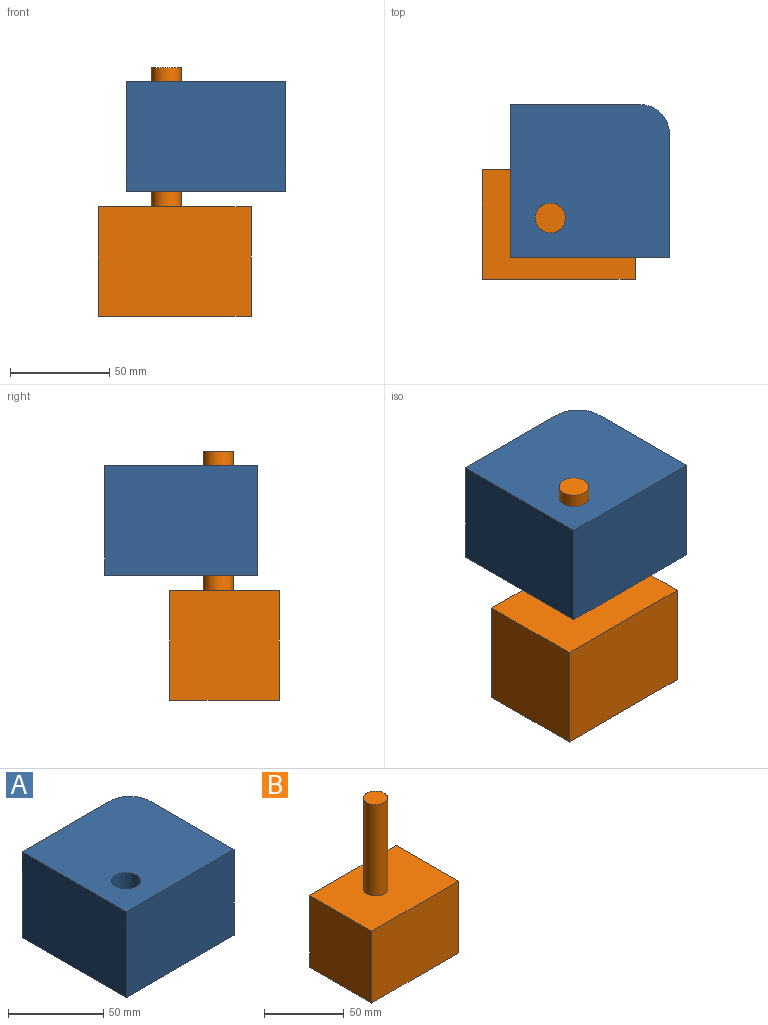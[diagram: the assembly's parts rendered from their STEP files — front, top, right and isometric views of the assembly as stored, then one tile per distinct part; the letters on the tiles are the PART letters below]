
ASSEMBLY  parts=2 mates=1
PART A: 8 faces, bbox 80x77.1x55 mm
  f0: plane 65x55mm, normal (0,1,0), area 3575mm2, adj f1,f4,f5,f7
  f1: plane 77.05x55mm, normal (-1,0,0), area 4237.9mm2, adj f0,f2,f4,f5
  f2: plane 80x55mm, normal (0,-1,0), area 4400mm2, adj f1,f3,f4,f5
  f3: plane 62.05x55mm, normal (1,0,0), area 3412.9mm2, adj f2,f4,f5,f7
  f4: plane 80x77.05mm, normal (0,0,1), area 5939.2mm2, adj f0,f1,f2,f3,f6,f7
  f5: plane 80x77.05mm, normal (0,0,-1), area 5939.2mm2, adj f0,f1,f2,f3,f6,f7
  f6: cylinder r=7.5mm len=55mm, axis (0,0,-1), area 2591.8mm2, adj f4,f5
  f7: cylinder r=15mm len=55mm, axis (0,0,-1), area 1295.9mm2, adj f0,f3,f4,f5
PART B: 8 faces, bbox 76.7x55x124.9 mm
  f0: plane 55x55mm, normal (-1,0,0), area 3025mm2, adj f1,f3,f4,f5
  f1: plane 76.74x55mm, normal (0,0,-1), area 4220.6mm2, adj f0,f2,f4,f5
  f2: plane 55x55mm, normal (1,0,0), area 3025mm2, adj f1,f3,f4,f5
  f3: plane 76.74x55mm, normal (0,0,1), area 4043.9mm2, adj f0,f2,f4,f5,f6
  f4: plane 76.74x55mm, normal (0,-1,0), area 4220.6mm2, adj f0,f1,f2,f3
  f5: plane 76.74x55mm, normal (0,1,0), area 4220.6mm2, adj f0,f1,f2,f3
  f6: cylinder r=7.5mm len=69.9mm, axis (0,0,-1), area 3294mm2, adj f3,f7
  f7: plane 15x15mm, normal (0,0,1), area 176.7mm2, adj f6
PLACE A t=(32.66,88.95,72.23)mm
PLACE B t=(16.95,94.73,36.81)mm
MATE cylindrical B.f6 <-> A.f6  axis (0,0,-1) through (12.66,70.42,99.26)mm
